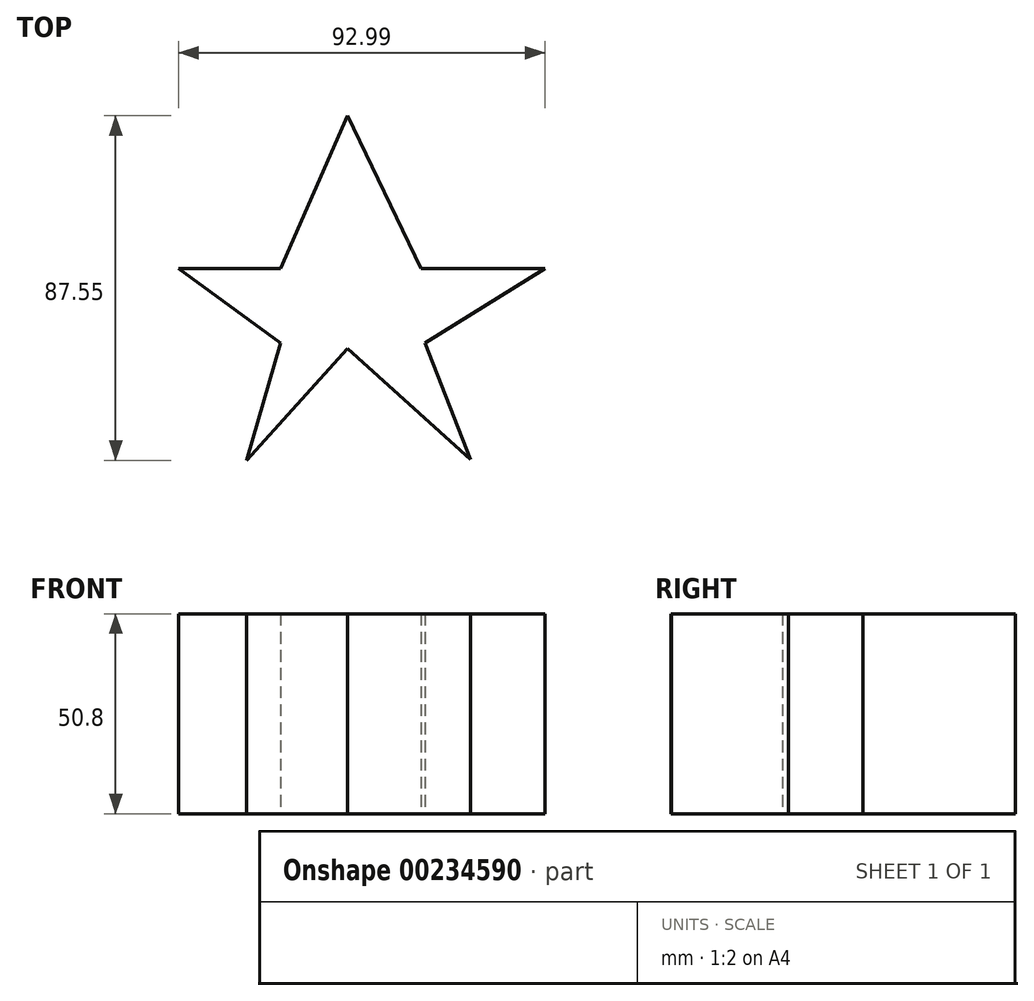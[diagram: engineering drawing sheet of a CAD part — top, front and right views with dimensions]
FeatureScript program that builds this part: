
annotation { "Feature Type Name" : "Feature", "Feature Type Description" : "" }
export const myFeature = defineFeature(function(context is Context, id is Id, definition is map)
    precondition{}
    {
        {
            var Q0;
            Q0=qCreatedBy(makeId("Top.planeOp"),FACE);
            var sketch = newSketch(context, id + "F0", { "sketchPlane" : qUnion([Q0])});
            skLineSegment(sketch, "E0", {"start": v(0, 38.76) * mm, "end": v(18.7, 0) * mm});
            skLineSegment(sketch, "E1", {"start": v(18.7, 0) * mm, "end": v(50.12, 0) * mm});
            skLineSegment(sketch, "E2", {"start": v(50.12, 0) * mm, "end": v(19.66, -18.93) * mm});
            skLineSegment(sketch, "E3", {"start": v(19.66, -18.93) * mm, "end": v(31.26, -48.59) * mm});
            skLineSegment(sketch, "E4", {"start": v(31.26, -48.59) * mm, "end": v(0, -20.39) * mm});
            skLineSegment(sketch, "E5", {"start": v(0, -20.39) * mm, "end": v(-25.63, -48.8) * mm});
            skLineSegment(sketch, "E6", {"start": v(-25.63, -48.8) * mm, "end": v(-17.08, -18.93) * mm});
            skLineSegment(sketch, "E7", {"start": v(-17.08, -18.93) * mm, "end": v(-42.87, 0) * mm});
            skLineSegment(sketch, "E8", {"start": v(-42.87, 0) * mm, "end": v(-17.08, 0) * mm});
            skLineSegment(sketch, "E9", {"start": v(-17.08, 0) * mm, "end": v(0, 38.76) * mm});
            skSolve(sketch);
        }
        {
            var Q0;
            Q0=makeQuery(id+"F0.imprint","IMPRINT",FACE,{"disambiguationData":[TD([[makeQuery(id+"F0.imprint","IMPRINT",EDGE,{"derivedFrom":sQuery(id+"F0.wireOp",EDGE,"E0")}),-1.0]])]});
            extrude(context, id + "F1", {"entities" : qUnion([Q0]), "depth" : 50.8 * mm});
        }
    });
